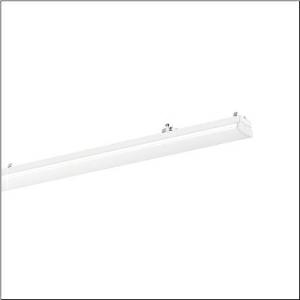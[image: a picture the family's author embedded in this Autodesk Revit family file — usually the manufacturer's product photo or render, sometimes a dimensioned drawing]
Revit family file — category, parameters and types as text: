
# Revit family: licross_r__21_recessed_opal_mo_52te1dmn46xg_b62e
name_source: partatom
category: Lighting Fixtures
units: mm (PartAtom-declared; Revit-internal decimal feet)

## family parameters
Cut with Voids When Loaded = No
Host = Face
Light Source = No
Part Type = Normal
Room Calculation Point = No
Round Connector Dimension = Use Diameter
Shared = No

## types (1)
- --- (1 x LED, 6270 lm, 35 W, 4000K)
    Apparent Load = 35 VA
    CIE Flux Codes = 44 73 91 87 100
    Color Rendering = 80
    Color Temperature = 4000K
    Default Elevation = 1800 mm
    Description = Licross® 21 recessed opal MO, luminaire insert, of sheet steel, galvanised, coil coated, white, length: 1.500mm, width: 66mm, height: 67mm, LED rated luminous flux: 6.270lm, light colour: 840, control gear: ON/OFF Multilumen, with plug, 3-pole, with phase selection, mains connection: 220..240V, AC, 50/60Hz, rated input power: 35W, internal wiring halogen-free, primary optical cover: cover, of PMMA, light emission: direct with ceiling illumination distribution, primary light characteristic: symmetric, protection rating (complete): IP54, insulation class (complete): insulation class I (protective earthing), certification: CE, ENEC, VDE, UKCA, protection symbol: D if used in an environment with non-conductive dust loads with corresponding accessories, impact resistance: IK06, permissible ambient temperature for indoor applications: -35..+50°C, corresponds to IFS (International Featured Standards) requirements for safety and quality in the food industry, reducing of maximum allowable ambient temperature of 5°C with ceiling mounting, LABS conformity tested according to VDMA 24364:2018-05, packaging unit: 1 piece
    Height = 83 mm
    Lamp = 1 x LED
    Lamp Light Flux = 6270 lm
    Lamp Power = 35 W
    Lamp count = 1
    Length = 1500 mm
    Luminous efficacy = 179 lm/W
    Manufacturer = Siteco
    ModVariant = No
    Model = 52TE1DMN46XG
    Mounting Place = Ceiling
    Mounting Type = Pendant
    Number of Poles = 1
    OnlyDefault = Yes
    Power Factor = 1
    Product Name = Licross® 21 recessed opal MO
    Product group = luminaire insert | ceiling pendant
    ProductGroupID = 902
    Protection Class = Protection class I
    Protection Degree = IP 54
    RLX_Detail_Level = 1
    RLX_Emergency_Light_Flux = 0 lm
    RLX_Emergency_Type = 0
    RLX_Emergency_Type_DB = No
    RlxData = <blob elided: 24737 chars, md5=dfdc26e3>
    Socket = socket
    Standby Power = 0 W
    System Light Flux = 6270 lm
    System Power = 35 W
    Type Comments = factory setting: luminous flux: 100 % | (A | C | E) | 81 mA
    Type Image = l_1313666.jpg
    URL = http://relux.com
    VarID = @adj_025767
    Voltage = 0 V
    Weight = 0.00 kg
    Width = 76 mm

## geometry (parser evidence)
native form markers: Blend x4, Sweep x12
no freeform markers — native parametric forms only
